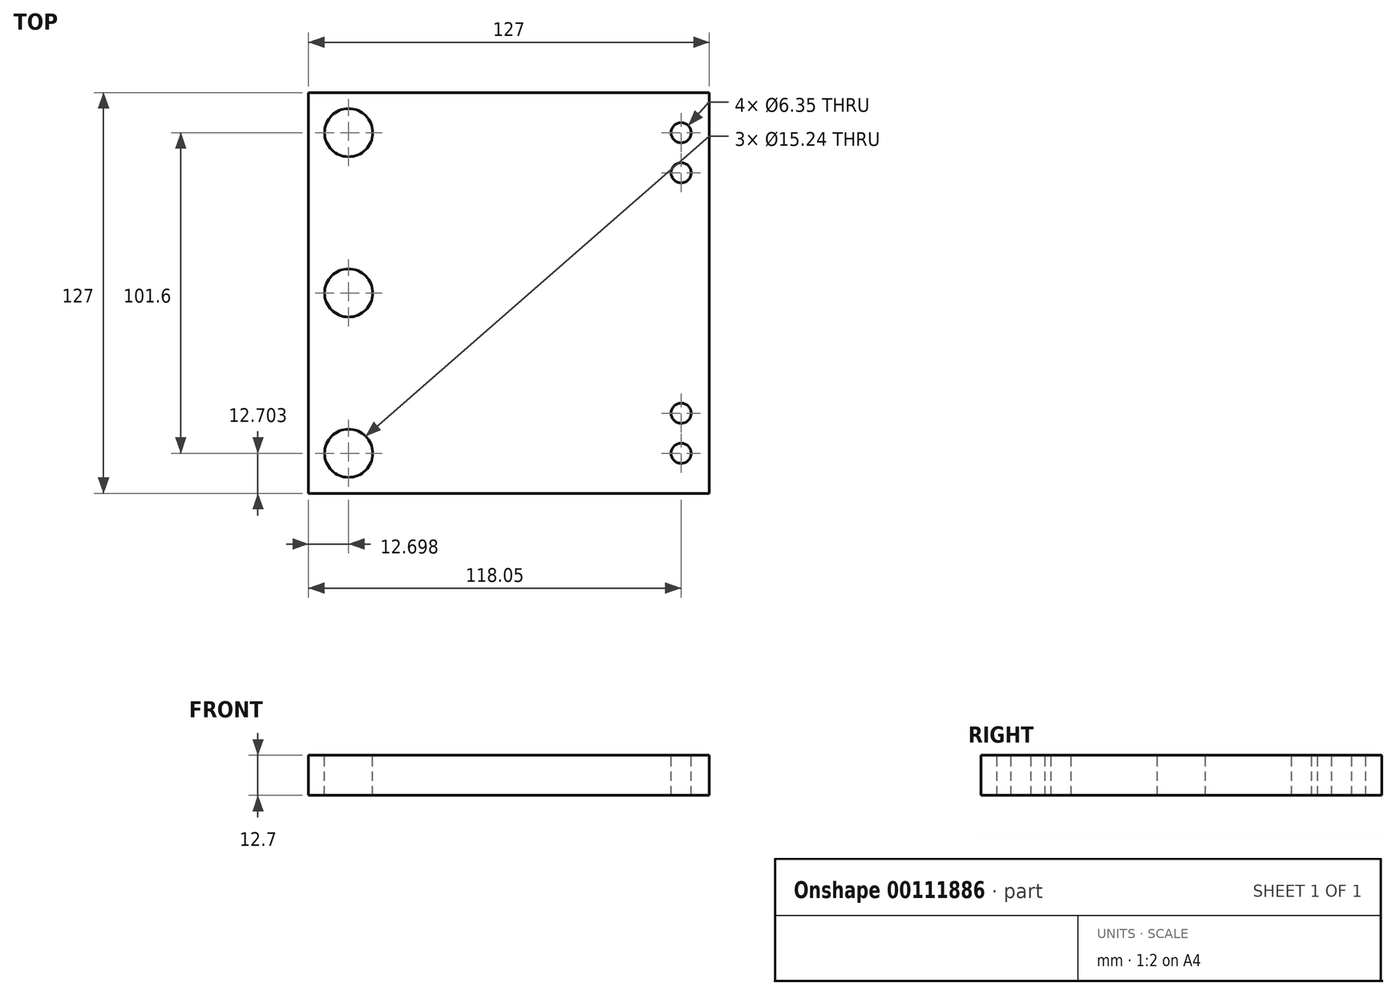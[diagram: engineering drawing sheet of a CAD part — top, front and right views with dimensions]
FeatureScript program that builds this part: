
annotation { "Feature Type Name" : "Feature", "Feature Type Description" : "" }
export const myFeature = defineFeature(function(context is Context, id is Id, definition is map)
    precondition{}
    {
        {
            var Q0;
            Q0=qCreatedBy(makeId("Top.planeOp"),FACE);
            var sketch = newSketch(context, id + "F0", { "sketchPlane" : qUnion([Q0])});
            skLineSegment(sketch, "E0.bottom", {"start": v(-53.22, 63.5) * mm, "end": v(73.78, 63.5) * mm});
            skLineSegment(sketch, "E0.top", {"start": v(-53.22, -63.5) * mm, "end": v(73.78, -63.5) * mm});
            skLineSegment(sketch, "E0.left", {"start": v(-53.22, 63.5) * mm, "end": v(-53.22, -63.5) * mm});
            skLineSegment(sketch, "E0.right", {"start": v(73.78, 63.5) * mm, "end": v(73.78, -63.5) * mm});
            skSolve(sketch);
        }
        {
            var Q0;
            Q0=makeQuery(id+"F0.imprint","IMPRINT",FACE,{"disambiguationData":[TD([[makeQuery(id+"F0.imprint","IMPRINT",EDGE,{"derivedFrom":sQuery(id+"F0.wireOp",EDGE,"E0.bottom")}),-1.0]])]});
            extrude(context, id + "F1", {"entities" : qUnion([Q0]), "depth" : 12.7 * mm});
        }
        {
            var Q0;
            Q0=makeQuery(id+"F1.opExtrude","CAP_FACE",FACE,{"disambiguationData":[OSD([sQuery(id+"F0.wireOp",EDGE,"E0.bottom"),sQuery(id+"F0.wireOp",EDGE,"E0.top"),sQuery(id+"F0.wireOp",EDGE,"E0.left"),sQuery(id+"F0.wireOp",EDGE,"E0.right")])],"isStart":false});
            var sketch = newSketch(context, id + "F2", { "sketchPlane" : qUnion([Q0])});
            skPoint(sketch, "E1", {"position": v(-40.52, 50.8) * mm});
            skPoint(sketch, "E2", {"position": v(-40.52, 0) * mm});
            skPoint(sketch, "E3", {"position": v(-40.52, -50.8) * mm});
            skSolve(sketch);
        }
        {
            var Q0;
            Q0=sQuery(id+"F2.wireOp",VERTEX,"E1");
            var Q1;
            Q1=sQuery(id+"F2.wireOp",VERTEX,"E2");
            var Q2;
            Q2=sQuery(id+"F2.wireOp",VERTEX,"E3");
            var Q3;
            Q3=makeQuery(id+"F1.opExtrude","SWEPT_BODY",BODY,{"disambiguationData":[OSD([sQuery(id+"F0.wireOp",EDGE,"E0.bottom"),sQuery(id+"F0.wireOp",EDGE,"E0.top"),sQuery(id+"F0.wireOp",EDGE,"E0.left"),sQuery(id+"F0.wireOp",EDGE,"E0.right")])]});
            hole(context, id + "F3", {"style" : HoleStyle.SIMPLE, "endStyle" : HoleEndStyle.BLIND, "holeDiameter" : 15.24 * mm, "holeDepth" : 12.7 * mm, "startFromSketch" : true, "locations" : qUnion([Q0, Q1, Q2]), "scope" : qUnion([Q3])});
        }
        {
            var Q0;
            Q0=makeQuery(id+"F1.opExtrude","CAP_FACE",FACE,{"disambiguationData":[OSD([sQuery(id+"F0.wireOp",EDGE,"E0.bottom"),sQuery(id+"F0.wireOp",EDGE,"E0.top"),sQuery(id+"F0.wireOp",EDGE,"E0.left"),sQuery(id+"F0.wireOp",EDGE,"E0.right")])],"isStart":false});
            var sketch = newSketch(context, id + "F4", { "sketchPlane" : qUnion([Q0])});
            skPoint(sketch, "E4", {"position": v(64.83, 50.8) * mm});
            skPoint(sketch, "E5", {"position": v(64.83, 38.1) * mm});
            skPoint(sketch, "E6", {"position": v(64.83, -50.8) * mm});
            skPoint(sketch, "E7", {"position": v(64.83, -38.1) * mm});
            skSolve(sketch);
        }
        {
            var Q0;
            Q0=sQuery(id+"F4.wireOp",VERTEX,"E7");
            var Q1;
            Q1=sQuery(id+"F4.wireOp",VERTEX,"E4");
            var Q2;
            Q2=sQuery(id+"F4.wireOp",VERTEX,"E5");
            var Q3;
            Q3=sQuery(id+"F4.wireOp",VERTEX,"E6");
            var Q4;
            Q4=makeQuery(id+"F1.opExtrude","SWEPT_BODY",BODY,{"disambiguationData":[OSD([sQuery(id+"F0.wireOp",EDGE,"E0.bottom"),sQuery(id+"F0.wireOp",EDGE,"E0.top"),sQuery(id+"F0.wireOp",EDGE,"E0.left"),sQuery(id+"F0.wireOp",EDGE,"E0.right")])]});
            hole(context, id + "F5", {"style" : HoleStyle.SIMPLE, "endStyle" : HoleEndStyle.BLIND, "holeDiameter" : 6.35 * mm, "holeDepth" : 12.7 * mm, "startFromSketch" : true, "locations" : qUnion([Q0, Q1, Q2, Q3]), "scope" : qUnion([Q4])});
        }
    });
